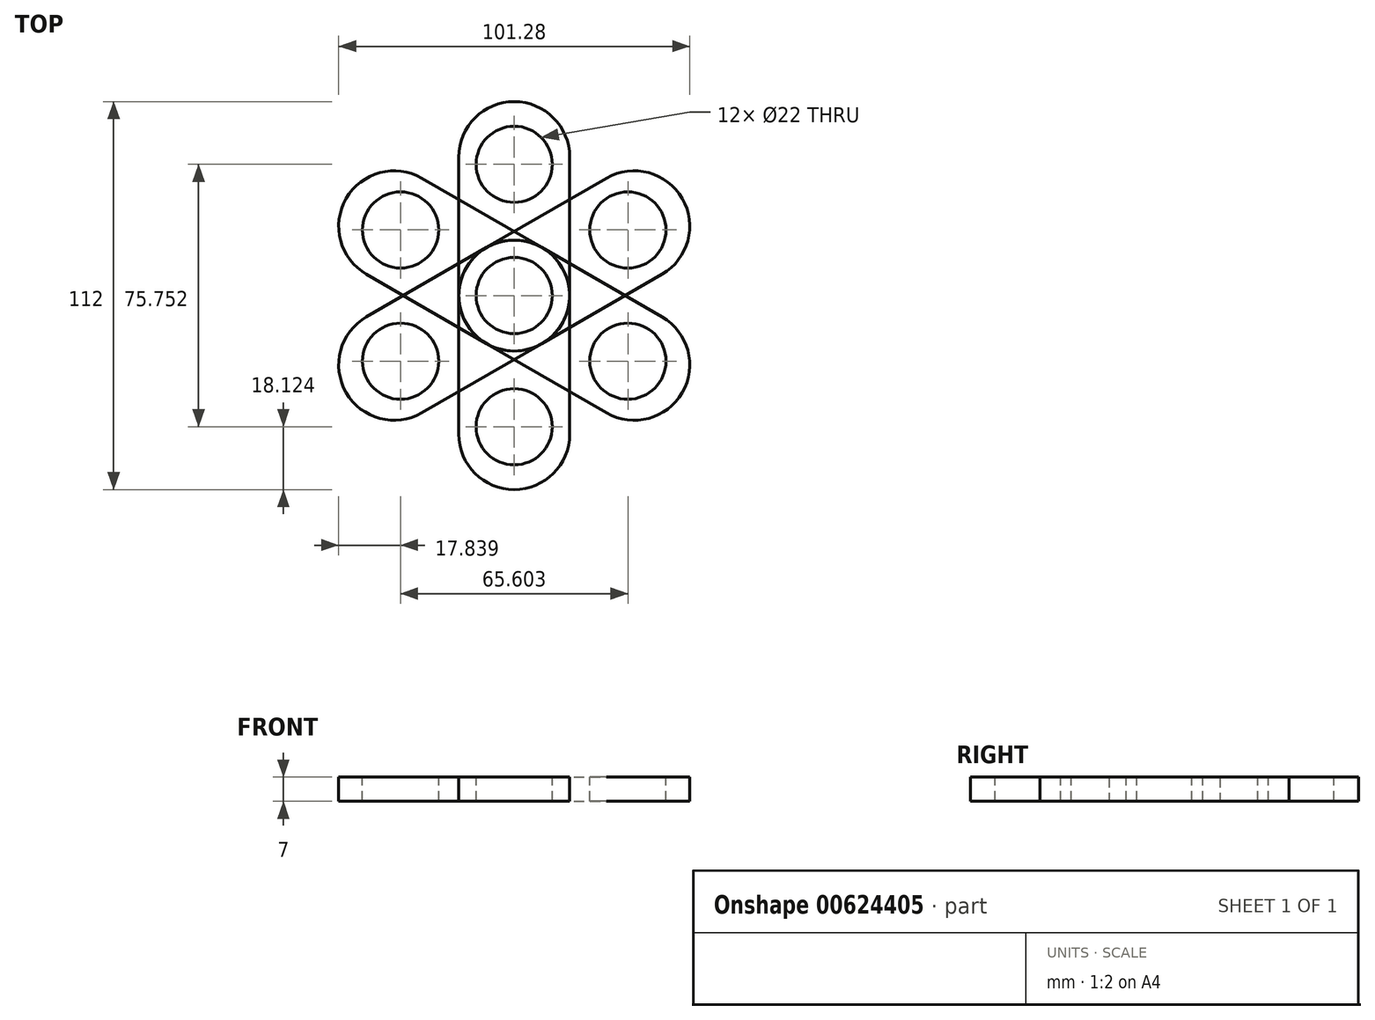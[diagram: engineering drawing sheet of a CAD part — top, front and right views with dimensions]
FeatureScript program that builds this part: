
annotation { "Feature Type Name" : "Feature", "Feature Type Description" : "" }
export const myFeature = defineFeature(function(context is Context, id is Id, definition is map)
    precondition{}
    {
        {
            var Q0;
            Q0=qCreatedBy(makeId("Top.planeOp"),FACE);
            var sketch = newSketch(context, id + "F0", { "sketchPlane" : qUnion([Q0])});
            skCircle(sketch, "E0", {"center": v(0, 0) * mm, "radius": 16 * mm});
            skCircle(sketch, "E1", {"center": v(0, -40) * mm, "radius": 16 * mm});
            skLineSegment(sketch, "E2", {"start": v(16, 0) * mm, "end": v(16, -40) * mm});
            skLineSegment(sketch, "E3", {"start": v(-16, 0) * mm, "end": v(-16, -40) * mm});
            skSolve(sketch);
        }
        {
            var Q0;
            Q0 = qSketchRegion(id + "F0", true);
            extrude(context, id + "F1", {"entities" : qUnion([Q0]), "depth" : 7 * mm, "offsetDistance" : 25 * mm});
        }
        {
            var Q0;
            Q0=makeQuery(id+"F1.opExtrude","CAP_FACE",FACE,{"disambiguationData":[OSD([sQuery(id+"F0.wireOp",EDGE,"E0"),sQuery(id+"F0.wireOp",EDGE,"E1"),sQuery(id+"F0.wireOp",EDGE,"E2"),sQuery(id+"F0.wireOp",EDGE,"E3")])],"isStart":false});
            var sketch = newSketch(context, id + "F2", { "sketchPlane" : qUnion([Q0])});
            skCircle(sketch, "E4", {"center": v(0, 0) * mm, "radius": 11 * mm});
            skCircle(sketch, "E5", {"center": v(0, -37.88) * mm, "radius": 11 * mm});
            skSolve(sketch);
        }
        {
            var Q0;
            Q0 = qSketchRegion(id + "F2", true);
            extrude(context, id + "F3", {"entities" : qUnion([Q0]), "operationType" : NewBodyOperationType.REMOVE, "endBound" : BoundingType.THROUGH_ALL, "oppositeDirection" : true, "depth" : 25 * mm, "offsetDistance" : 25 * mm});
        }
        {
            var Q0;
            Q0=qCreatedBy(makeId("Front.planeOp"),FACE);
            var sketch = newSketch(context, id + "F4", { "sketchPlane" : qUnion([Q0])});
            skLineSegment(sketch, "E6", {"start": v(0, 0) * mm, "end": v(0, 26.48) * mm});
            skSolve(sketch);
        }
        {
            var Q0;
            Q0=makeQuery(id+"F1.opExtrude","SWEPT_BODY",BODY,{"disambiguationData":[OSD([sQuery(id+"F0.wireOp",EDGE,"E0"),sQuery(id+"F0.wireOp",EDGE,"E1"),sQuery(id+"F0.wireOp",EDGE,"E2"),sQuery(id+"F0.wireOp",EDGE,"E3")])]});
            var Q1;
            Q1=sQuery(id+"F4.wireOp",EDGE,"E6");
            circularPattern(context, id + "F5", {"entities" : qUnion([Q0]), "axis" : qUnion([Q1]), "angle" : 360 * degree, "instanceCount" : 6, "equalSpace" : true});
        }
    });
